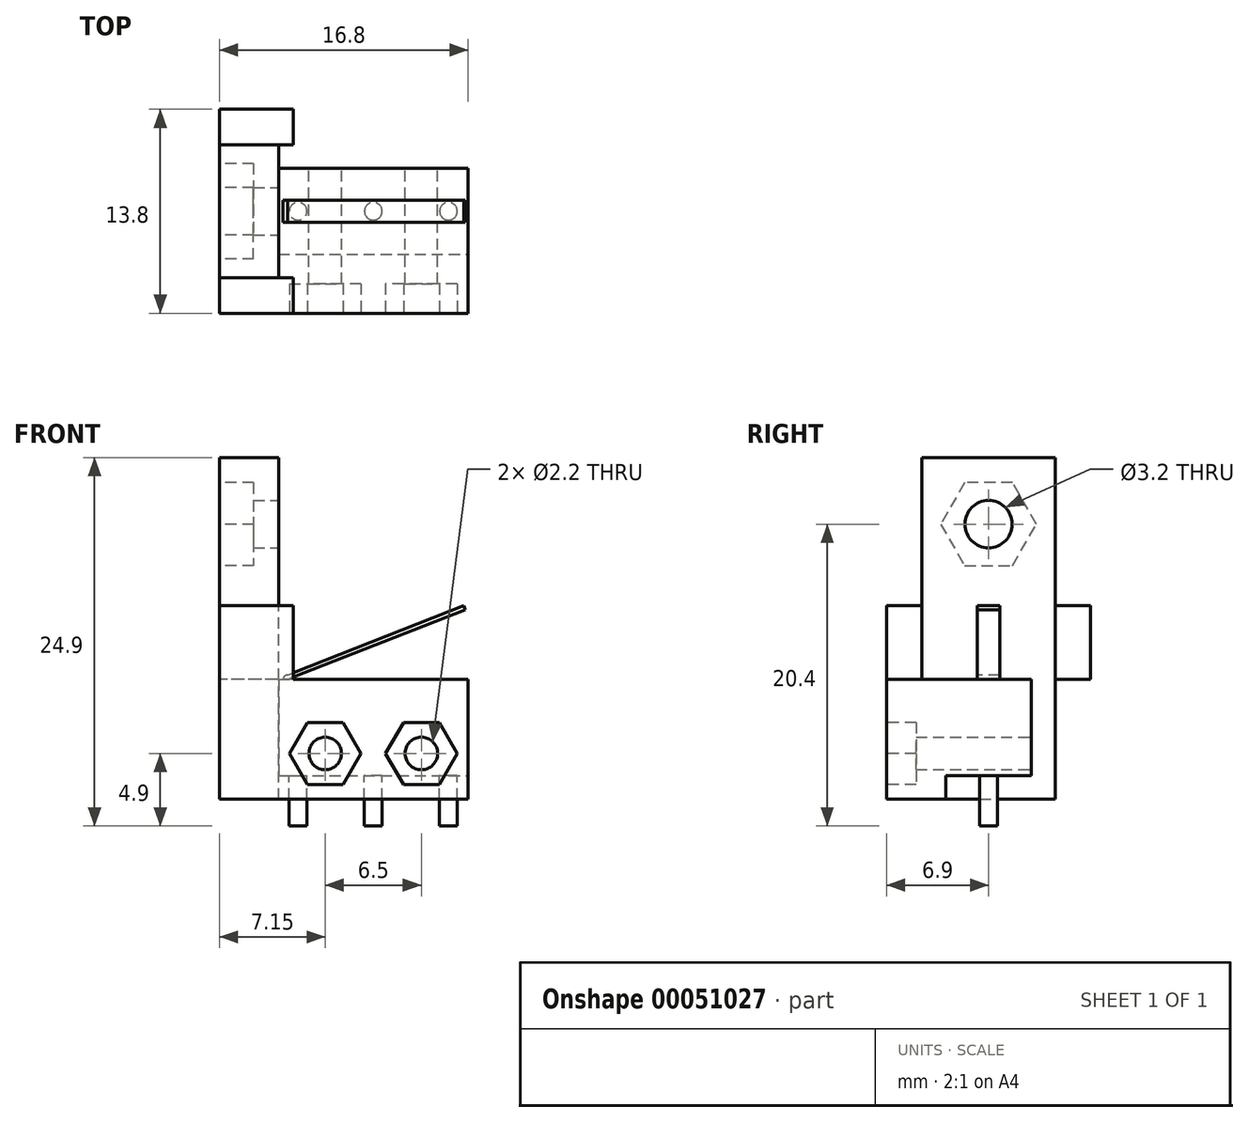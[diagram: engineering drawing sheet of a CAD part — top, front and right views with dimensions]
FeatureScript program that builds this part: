
annotation { "Feature Type Name" : "Feature", "Feature Type Description" : "" }
export const myFeature = defineFeature(function(context is Context, id is Id, definition is map)
    precondition{}
    {
        {
            var Q0;
            Q0=qCreatedBy(makeId("Front.planeOp"),FACE);
            var sketch = newSketch(context, id + "F0", { "sketchPlane" : qUnion([Q0])});
            skLineSegment(sketch, "E0.bottom", {"start": v(-6.4, 6.5) * mm, "end": v(6.4, 6.5) * mm});
            skLineSegment(sketch, "E0.top", {"start": v(-6.4, 0) * mm, "end": v(6.4, 0) * mm});
            skLineSegment(sketch, "E0.left", {"start": v(-6.4, 6.5) * mm, "end": v(-6.4, 0) * mm});
            skLineSegment(sketch, "E0.right", {"start": v(6.4, 6.5) * mm, "end": v(6.4, 0) * mm});
            skCircle(sketch, "E1", {"center": v(3.25, 1.5) * mm, "radius": 1.1 * mm});
            skCircle(sketch, "E2", {"center": v(-3.25, 1.5) * mm, "radius": 1.1 * mm});
            skLineSegment(sketch, "E3", {"start": v(0, 0.48) * mm, "end": v(0, 13.87) * mm, "construction": true});
            skSolve(sketch);
        }
        {
            var Q0;
            Q0 = qSketchRegion(id + "F0", true);
            extrude(context, id + "F1", {"entities" : qUnion([Q0]), "depth" : 5.8 * mm});
        }
        {
            var Q0;
            Q0=makeQuery(id+"F1.opExtrude","SWEPT_FACE",FACE,{"disambiguationData":[OSD([sQuery(id+"F0.wireOp",EDGE,"E0.top")])]});
            var sketch = newSketch(context, id + "F2", { "sketchPlane" : qUnion([Q0])});
            skLineSegment(sketch, "E4", {"start": v(0, 12.32) * mm, "end": v(0, -7.08) * mm, "construction": true});
            skCircle(sketch, "E5", {"center": v(-5.08, 2.9) * mm, "radius": 0.6 * mm});
            skCircle(sketch, "E6", {"center": v(0, 2.9) * mm, "radius": 0.6 * mm});
            skCircle(sketch, "E7", {"center": v(5.08, 2.9) * mm, "radius": 0.6 * mm});
            skLineSegment(sketch, "E8", {"start": v(-20.59, 2.9) * mm, "end": v(16.53, 2.9) * mm, "construction": true});
            skPoint(sketch, "E9", {"position": v(-6.4, 2.9) * mm});
            skSolve(sketch);
        }
        {
            var Q0;
            Q0 = qSketchRegion(id + "F2", true);
            extrude(context, id + "F3", {"entities" : qUnion([Q0]), "operationType" : NewBodyOperationType.ADD, "depth" : 3.4 * mm});
        }
        {
            var Q0;
            Q0=makeQuery(id+"F1.opExtrude","CAP_FACE",FACE,{"disambiguationData":[OSD([sQuery(id+"F0.wireOp",EDGE,"E0.bottom"),sQuery(id+"F0.wireOp",EDGE,"E0.top"),sQuery(id+"F0.wireOp",EDGE,"E0.left"),sQuery(id+"F0.wireOp",EDGE,"E0.right"),sQuery(id+"F0.wireOp",EDGE,"E1"),sQuery(id+"F0.wireOp",EDGE,"E2")])],"isStart":true});
            var Q1;
            Q1=makeQuery(id+"F1.opExtrude","CAP_FACE",FACE,{"disambiguationData":[OSD([sQuery(id+"F0.wireOp",EDGE,"E0.bottom"),sQuery(id+"F0.wireOp",EDGE,"E0.top"),sQuery(id+"F0.wireOp",EDGE,"E0.left"),sQuery(id+"F0.wireOp",EDGE,"E0.right"),sQuery(id+"F0.wireOp",EDGE,"E1"),sQuery(id+"F0.wireOp",EDGE,"E2")])],"isStart":false});
            cPlane(context, id + "F4", {"entities" : qUnion([Q0, Q1]), "cplaneType" : CPlaneType.MID_PLANE, "offset" : 150 * mm, "width" : 150 * mm, "height" : 150 * mm});
        }
        {
            var Q0;
            Q0=qCreatedBy(id+"F4.planeOp",FACE);
            var sketch = newSketch(context, id + "F5", { "sketchPlane" : qUnion([Q0])});
            skLineSegment(sketch, "E10", {"start": v(16.26, 6.5) * mm, "end": v(-15.15, 6.5) * mm, "construction": true});
            skLineSegment(sketch, "E11", {"start": v(5.8, 6.5) * mm, "end": v(-6.22, 11.22) * mm});
            skLineSegment(sketch, "E12", {"start": v(5.8, 6.8) * mm, "end": v(-6.1, 11.5) * mm});
            skLineSegment(sketch, "E13", {"start": v(-6.1, 11.5) * mm, "end": v(-6.22, 11.22) * mm});
            skLineSegment(sketch, "E14", {"start": v(5.8, 6.5) * mm, "end": v(6.1, 6.5) * mm});
            skArc(sketch, "E15", {"start": v(6.1, 6.5) * mm, "mid": v(6.01, 6.71) * mm, "end": v(5.8, 6.8) * mm});
            skLineSegment(sketch, "E16", {"start": v(5.8, 6.5) * mm, "end": v(5.8, 6.8) * mm, "construction": true});
            skLineSegment(sketch, "E17", {"start": v(15.7, 1.5) * mm, "end": v(-17.73, 1.5) * mm, "construction": true});
            skPoint(sketch, "E18", {"position": v(-3.25, 1.5) * mm});
            skPoint(sketch, "E19", {"position": v(3.25, 1.5) * mm});
            skSolve(sketch);
        }
        {
            var Q0;
            Q0 = qSketchRegion(id + "F5", true);
            extrude(context, id + "F6", {"entities" : qUnion([Q0]), "operationType" : NewBodyOperationType.ADD, "endBound" : BoundingType.SYMMETRIC, "depth" : 1.5 * mm});
        }
        {
            var Q0;
            Q0=makeQuery(id+"F1.opExtrude","CAP_FACE",FACE,{"disambiguationData":[OSD([sQuery(id+"F0.wireOp",EDGE,"E0.bottom"),sQuery(id+"F0.wireOp",EDGE,"E0.top"),sQuery(id+"F0.wireOp",EDGE,"E0.left"),sQuery(id+"F0.wireOp",EDGE,"E0.right"),sQuery(id+"F0.wireOp",EDGE,"E1"),sQuery(id+"F0.wireOp",EDGE,"E2")])],"isStart":false});
            var sketch = newSketch(context, id + "F7", { "sketchPlane" : qUnion([Q0])});
            skLineSegment(sketch, "E20.bottom", {"start": v(6.4, -1.6) * mm, "end": v(-6.4, -1.6) * mm});
            skLineSegment(sketch, "E20.top", {"start": v(6.4, 6.5) * mm, "end": v(-6.4, 6.5) * mm});
            skLineSegment(sketch, "E20.left", {"start": v(6.4, -1.6) * mm, "end": v(6.4, 6.5) * mm});
            skLineSegment(sketch, "E20.right", {"start": v(-6.4, -1.6) * mm, "end": v(-6.4, 6.5) * mm});
            skLineSegment(sketch, "E21", {"start": v(0, -13.07) * mm, "end": v(0, 21.12) * mm, "construction": true});
            skPoint(sketch, "E22", {"position": v(3.25, 1.5) * mm});
            skPoint(sketch, "E23", {"position": v(-3.25, 1.5) * mm});
            skLineSegment(sketch, "E24", {"start": v(3.25, 1.5) * mm, "end": v(-3.25, 1.5) * mm, "construction": true});
            skCircle(sketch, "E25", {"center": v(3.25, 1.5) * mm, "radius": 1.1 * mm});
            skCircle(sketch, "E26", {"center": v(-3.25, 1.5) * mm, "radius": 1.1 * mm});
            skSolve(sketch);
        }
        {
            var Q0;
            Q0 = qSketchRegion(id + "F7", true);
            extrude(context, id + "F8", {"entities" : qUnion([Q0]), "depth" : 4 * mm});
        }
        {
            var Q0;
            Q0=makeQuery(id+"F8.opExtrude","CAP_FACE",FACE,{"disambiguationData":[OSD([sQuery(id+"F7.wireOp",EDGE,"E20.bottom"),sQuery(id+"F7.wireOp",EDGE,"E20.top"),sQuery(id+"F7.wireOp",EDGE,"E20.left"),sQuery(id+"F7.wireOp",EDGE,"E20.right")])],"isStart":false});
            var sketch = newSketch(context, id + "F9", { "sketchPlane" : qUnion([Q0])});
            skLineSegment(sketch, "E27", {"start": v(-3.25, -7.44) * mm, "end": v(-3.25, 10.28) * mm, "construction": true});
            skCircle(sketch, "E28.cCircle", {"center": v(-3.25, 1.5) * mm, "radius": 2.1 * mm, "construction": true});
            skLineSegment(sketch, "E28.0", {"start": v(-2.04, -0.6) * mm, "end": v(-4.46, -0.6) * mm});
            skLineSegment(sketch, "E28.1", {"start": v(-4.46, -0.6) * mm, "end": v(-5.67, 1.5) * mm});
            skLineSegment(sketch, "E28.2", {"start": v(-5.67, 1.5) * mm, "end": v(-4.46, 3.6) * mm});
            skLineSegment(sketch, "E28.3", {"start": v(-4.46, 3.6) * mm, "end": v(-2.04, 3.6) * mm});
            skLineSegment(sketch, "E28.4", {"start": v(-2.04, 3.6) * mm, "end": v(-0.83, 1.5) * mm});
            skLineSegment(sketch, "E28.5", {"start": v(-0.83, 1.5) * mm, "end": v(-2.04, -0.6) * mm});
            skPoint(sketch, "E28.0.midPoint", {"position": v(-3.25, -0.6) * mm});
            skLineSegment(sketch, "E29", {"start": v(0, -5.2) * mm, "end": v(0, 11) * mm, "construction": true});
            skLineSegment(sketch, "E30.MirrorCS", {"start": v(0.83, 1.5) * mm, "end": v(2.04, -0.6) * mm});
            skPoint(sketch, "E31.MirrorP", {"position": v(3.25, -0.6) * mm});
            skLineSegment(sketch, "E32.MirrorCS", {"start": v(5.67, 1.5) * mm, "end": v(4.46, 3.6) * mm});
            skLineSegment(sketch, "E33.MirrorCS", {"start": v(4.46, 3.6) * mm, "end": v(2.04, 3.6) * mm});
            skLineSegment(sketch, "E34.MirrorCS", {"start": v(2.04, 3.6) * mm, "end": v(0.83, 1.5) * mm});
            skCircle(sketch, "E35.MirrorC", {"center": v(3.25, 1.5) * mm, "radius": 2.1 * mm, "construction": true});
            skLineSegment(sketch, "E36.MirrorCS", {"start": v(4.46, -0.6) * mm, "end": v(5.67, 1.5) * mm});
            skLineSegment(sketch, "E37.MirrorCS", {"start": v(2.04, -0.6) * mm, "end": v(4.46, -0.6) * mm});
            skSolve(sketch);
        }
        {
            var Q0;
            Q0 = qSketchRegion(id + "F9", true);
            extrude(context, id + "F10", {"entities" : qUnion([Q0]), "operationType" : NewBodyOperationType.REMOVE, "oppositeDirection" : true, "depth" : 2 * mm});
        }
        {
            var Q0;
            Q0=makeQuery(id+"F1.opExtrude","SWEPT_FACE",FACE,{"disambiguationData":[OSD([sQuery(id+"F0.wireOp",EDGE,"E0.left")])]});
            var sketch = newSketch(context, id + "F11", { "sketchPlane" : qUnion([Q0])});
            skLineSegment(sketch, "E38.top", {"start": v(7.4, 21.5) * mm, "end": v(-1.6, 21.5) * mm});
            skLineSegment(sketch, "E38.left", {"start": v(7.4, 6.5) * mm, "end": v(7.4, 21.5) * mm});
            skLineSegment(sketch, "E38.right", {"start": v(-1.6, -1.6) * mm, "end": v(-1.6, 21.5) * mm});
            skLineSegment(sketch, "E39", {"start": v(2.9, 5.34) * mm, "end": v(2.9, 57.94) * mm, "construction": true});
            skLineSegment(sketch, "E40", {"start": v(7.4, 6.5) * mm, "end": v(9.8, 6.5) * mm});
            skLineSegment(sketch, "E41", {"start": v(9.8, 6.5) * mm, "end": v(9.8, -1.6) * mm});
            skLineSegment(sketch, "E42", {"start": v(9.8, -1.6) * mm, "end": v(-1.6, -1.6) * mm});
            skPoint(sketch, "E43", {"position": v(2.9, 21.5) * mm});
            skLineSegment(sketch, "E44", {"start": v(18.07, 9.5) * mm, "end": v(-14.2, 9.5) * mm, "construction": true});
            skCircle(sketch, "E45", {"center": v(2.9, 17) * mm, "radius": 1.6 * mm});
            skSolve(sketch);
        }
        {
            var Q0;
            Q0 = qSketchRegion(id + "F11", true);
            extrude(context, id + "F12", {"entities" : qUnion([Q0]), "operationType" : NewBodyOperationType.ADD, "depth" : 4 * mm});
        }
        {
            var Q0;
            Q0=makeQuery(id+"F12.opExtrude","CAP_FACE",FACE,{"disambiguationData":[OSD([sQuery(id+"F11.wireOp",EDGE,"E38.top"),sQuery(id+"F11.wireOp",EDGE,"E38.left"),sQuery(id+"F11.wireOp",EDGE,"E38.right"),sQuery(id+"F11.wireOp",EDGE,"E40"),sQuery(id+"F11.wireOp",EDGE,"E41"),sQuery(id+"F11.wireOp",EDGE,"E42"),sQuery(id+"F11.wireOp",EDGE,"E45")])],"isStart":false});
            var sketch = newSketch(context, id + "F13", { "sketchPlane" : qUnion([Q0])});
            skLineSegment(sketch, "E46", {"start": v(2.9, 27.74) * mm, "end": v(2.9, 6.94) * mm, "construction": true});
            skPoint(sketch, "E47", {"position": v(2.9, 17) * mm});
            skCircle(sketch, "E48.cCircle", {"center": v(2.9, 17) * mm, "radius": 2.8 * mm, "construction": true});
            skLineSegment(sketch, "E48.0", {"start": v(4.52, 14.2) * mm, "end": v(1.28, 14.2) * mm});
            skLineSegment(sketch, "E48.1", {"start": v(1.28, 14.2) * mm, "end": v(-0.33, 17) * mm});
            skLineSegment(sketch, "E48.2", {"start": v(-0.33, 17) * mm, "end": v(1.28, 19.8) * mm});
            skLineSegment(sketch, "E48.3", {"start": v(1.28, 19.8) * mm, "end": v(4.52, 19.8) * mm});
            skLineSegment(sketch, "E48.4", {"start": v(4.52, 19.8) * mm, "end": v(6.13, 17) * mm});
            skLineSegment(sketch, "E48.5", {"start": v(6.13, 17) * mm, "end": v(4.52, 14.2) * mm});
            skPoint(sketch, "E48.0.midPoint", {"position": v(2.9, 14.2) * mm});
            skSolve(sketch);
        }
        {
            var Q0;
            Q0 = qSketchRegion(id + "F13", true);
            extrude(context, id + "F14", {"entities" : qUnion([Q0]), "operationType" : NewBodyOperationType.REMOVE, "oppositeDirection" : true, "depth" : 2.3 * mm});
        }
        {
            var Q0;
            Q0=makeQuery(id+"F12.opExtrude","CAP_FACE",FACE,{"disambiguationData":[OSD([sQuery(id+"F11.wireOp",EDGE,"E38.top"),sQuery(id+"F11.wireOp",EDGE,"E38.left"),sQuery(id+"F11.wireOp",EDGE,"E38.right"),sQuery(id+"F11.wireOp",EDGE,"E40"),sQuery(id+"F11.wireOp",EDGE,"E41"),sQuery(id+"F11.wireOp",EDGE,"E42"),sQuery(id+"F11.wireOp",EDGE,"E45")])],"isStart":false});
            var sketch = newSketch(context, id + "F15", { "sketchPlane" : qUnion([Q0])});
            skLineSegment(sketch, "E49", {"start": v(2.9, -3.9) * mm, "end": v(2.9, 26.18) * mm, "construction": true});
            skLineSegment(sketch, "E50.bottom", {"start": v(9.8, 6.5) * mm, "end": v(7.4, 6.5) * mm});
            skLineSegment(sketch, "E50.top", {"start": v(9.8, 11.5) * mm, "end": v(7.4, 11.5) * mm});
            skLineSegment(sketch, "E50.left", {"start": v(9.8, 6.5) * mm, "end": v(9.8, 11.5) * mm});
            skLineSegment(sketch, "E50.right", {"start": v(7.4, 6.5) * mm, "end": v(7.4, 11.5) * mm});
            skLineSegment(sketch, "E51.MirrorCS", {"start": v(-1.6, 6.5) * mm, "end": v(-1.6, 11.5) * mm});
            skLineSegment(sketch, "E52.MirrorCS", {"start": v(-4, 6.5) * mm, "end": v(-1.6, 6.5) * mm});
            skLineSegment(sketch, "E53.MirrorCS", {"start": v(-4, 11.5) * mm, "end": v(-1.6, 11.5) * mm});
            skLineSegment(sketch, "E54.MirrorCS", {"start": v(-4, 6.5) * mm, "end": v(-4, 11.5) * mm});
            skSolve(sketch);
        }
        {
            var Q0;
            Q0 = qSketchRegion(id + "F15", true);
            extrude(context, id + "F16", {"entities" : qUnion([Q0]), "operationType" : NewBodyOperationType.ADD, "oppositeDirection" : true, "depth" : (4 + 1) * mm});
        }
    });
